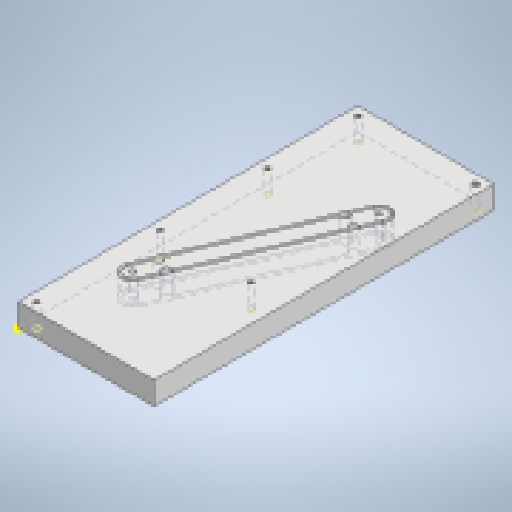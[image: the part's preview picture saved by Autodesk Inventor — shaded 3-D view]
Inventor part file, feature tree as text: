
AUTODESK INVENTOR PART (.ipt)
format: ipt  version: 2023 (Build 270158000, 158)  size: 227,840 bytes
history: native  units: mm
features: reference x9, thread x6, sketch x4, extrude x3, other x3
ambient origin geometry x8: Origin, YZ Plane, XZ Plane, XY Plane, X Axis, Y Axis, Z Axis, Center Point
bodies: Solid1 (feature_tree)
feature tree (25):
  extrude  "Extrusion1"  Depth=60.0mm
  sketch  "Sketch2"  dims[d2=10.0mm d3=0.0mm d4=2.2mm d5=2.2mm d6=2.2mm d7=2.2mm d8=2.2mm d9=2.2mm d10=10.0mm d11=0.0mm]
  extrude  "Extrusion2"  Depth=10.0mm
  thread  "Thread1"  [1 undecoded]
  thread  "Thread2"  [1 undecoded]
  thread  "Thread3"  [1 undecoded]
  thread  "Thread4"  [1 undecoded]
  thread  "Thread5"  [1 undecoded]
  thread  "Thread6"  [1 undecoded]
  extrude  "Extrusion3"  Depth=10.0mm TaperAngle=0.0deg
  sketch  "Sketch1"  dims[d0=150.0mm d1=60.0mm]
  reference  "Reference1"
  reference  "Reference2"
  reference  "Reference3"
  reference  "Reference4"
  reference  "Reference5"
  reference  "Reference6"
  sketch  "Sketch3"  dims[d12=10.0mm d13=0.0mm d14=10.0mm d15=0.0mm]
  sketch  "Sketch4"  dims[d16=10.0mm d17=0.0mm d18=10.0mm d19=0.0mm d20=10.0mm d21=0.0mm d22=10.0mm d23=0.0mm d24=10.0mm d25=22.5mm d26=35.0mm d27=35.0mm d28=7.0mm d29=7.0mm d30=4.0mm d31=4.0mm d32=90.0deg d33=4.0mm d34=4.0mm d35=10.0mm d36=10.0mm d37=10.0mm d38=0.0mm d39=2.2mm d40=2.2mm]
  reference  "Reference7"
  reference  "Reference8"
  reference  "Reference9"
  other  "<userpath>\ClawdDrive\Objet3D\IminaProbe\V2\FlexK7V2.iam"
  other  "FlexK7V2.iam"
  other  "FlexK7V2:1"
note: 6 required parameter values undecoded (feature->parameter linkage not recoverable at this tier; creation-order binding heuristic only, values carry confidence <= 0.55)
